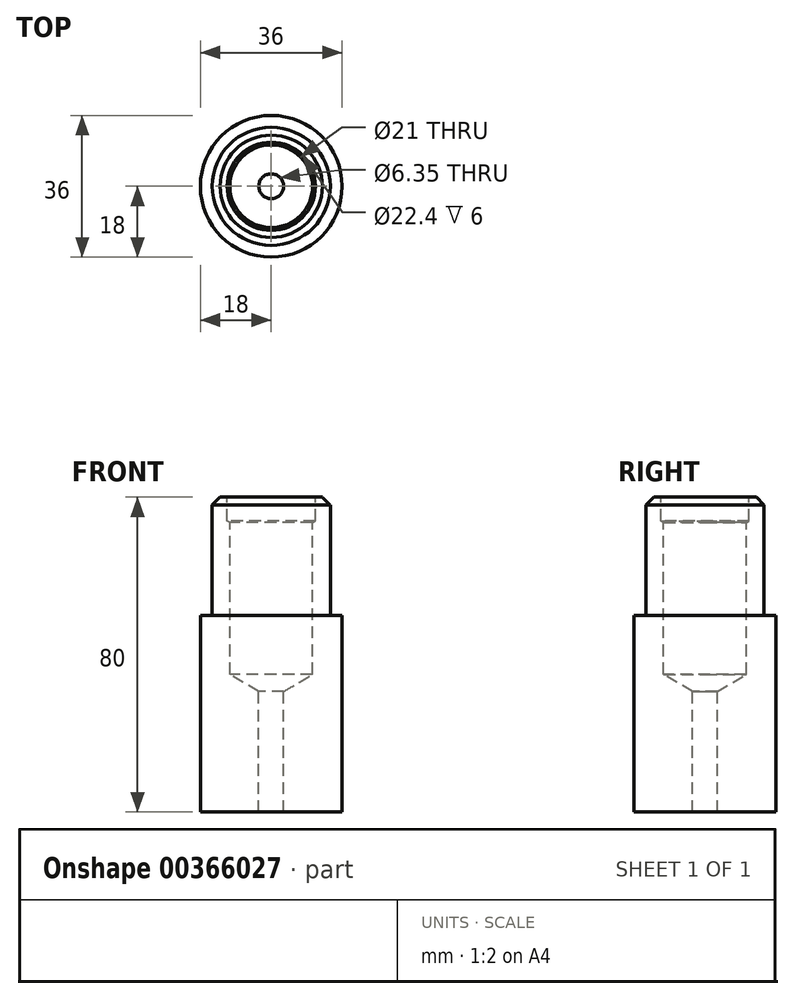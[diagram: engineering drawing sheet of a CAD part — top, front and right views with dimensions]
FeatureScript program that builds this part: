
annotation { "Feature Type Name" : "Feature", "Feature Type Description" : "" }
export const myFeature = defineFeature(function(context is Context, id is Id, definition is map)
    precondition{}
    {
        {
            var Q0;
            Q0=qCreatedBy(makeId("Top.planeOp"),FACE);
            var sketch = newSketch(context, id + "F0", { "sketchPlane" : qUnion([Q0])});
            skCircle(sketch, "E0", {"center": v(0, 0) * mm, "radius": 15 * mm});
            skSolve(sketch);
        }
        {
            var Q0;
            Q0=makeQuery(id+"F0.imprint","IMPRINT",FACE,{"disambiguationData":[TD([[makeQuery(id+"F0.imprint","IMPRINT",EDGE,{"derivedFrom":sQuery(id+"F0.wireOp",EDGE,"E0")}),1.0]])]});
            extrude(context, id + "F1", {"entities" : qUnion([Q0]), "depth" : 80 * mm});
        }
        {
            var Q0;
            Q0=qCreatedBy(makeId("Top.planeOp"),FACE);
            var sketch = newSketch(context, id + "F2", { "sketchPlane" : qUnion([Q0])});
            skCircle(sketch, "E1", {"center": v(0, 0) * mm, "radius": 18 * mm});
            skSolve(sketch);
        }
        {
            var Q0;
            Q0=makeQuery(id+"F2.imprint","IMPRINT",FACE,{"disambiguationData":[TD([[makeQuery(id+"F2.imprint","IMPRINT",EDGE,{"derivedFrom":sQuery(id+"F2.wireOp",EDGE,"E1")}),1.0]])]});
            extrude(context, id + "F3", {"entities" : qUnion([Q0]), "operationType" : NewBodyOperationType.ADD, "depth" : 50 * mm});
        }
        {
            var Q0;
            Q0=makeQuery(id+"F1.opExtrude","CAP_FACE",FACE,{"disambiguationData":[OSD([sQuery(id+"F0.wireOp",EDGE,"E0")])],"isStart":false});
            cPlane(context, id + "F4", {"entities" : qUnion([Q0]), "cplaneType" : CPlaneType.OFFSET, "offset" : 0 * mm, "width" : 150 * mm, "height" : 150 * mm});
        }
        {
            var Q0;
            Q0=qCreatedBy(id+"F4.planeOp",FACE);
            var sketch = newSketch(context, id + "F5", { "sketchPlane" : qUnion([Q0])});
            skPoint(sketch, "E2", {"position": v(0, 0) * mm});
            skSolve(sketch);
        }
        {
            var Q0;
            Q0=sQuery(id+"F5.wireOp",VERTEX,"E2");
            var Q1;
            Q1=makeQuery(id+"F1.opExtrude","SWEPT_BODY",BODY,{"disambiguationData":[OSD([sQuery(id+"F0.wireOp",EDGE,"E0")])]});
            hole(context, id + "F6", {"style" : HoleStyle.SIMPLE, "endStyle" : HoleEndStyle.THROUGH, "holeDiameter" : 6.35 * mm, "isTappedThrough" : true, "tappedDepth" : 12 * mm, "tapClearance" : 3, "startFromSketch" : true, "locations" : qUnion([Q0]), "scope" : qUnion([Q1])});
        }
        {
            var Q0;
            Q0=qCreatedBy(id+"F4.planeOp",FACE);
            var sketch = newSketch(context, id + "F7", { "sketchPlane" : qUnion([Q0])});
            skPoint(sketch, "E3", {"position": v(0, 0) * mm});
            skSolve(sketch);
        }
        {
            var Q0;
            Q0=sQuery(id+"F7.wireOp",VERTEX,"E3");
            var Q1;
            Q1=makeQuery(id+"F1.opExtrude","SWEPT_BODY",BODY,{"disambiguationData":[OSD([sQuery(id+"F0.wireOp",EDGE,"E0")])]});
            hole(context, id + "F8", {"style" : HoleStyle.SIMPLE, "endStyle" : HoleEndStyle.BLIND, "holeDiameter" : 21 * mm, "holeDepth" : 45 * mm, "isTappedThrough" : true, "tappedDepth" : 12 * mm, "tapClearance" : 3, "startFromSketch" : true, "locations" : qUnion([Q0]), "scope" : qUnion([Q1])});
        }
        {
            var Q0;
            Q0=qCreatedBy(id+"F4.planeOp",FACE);
            var sketch = newSketch(context, id + "F9", { "sketchPlane" : qUnion([Q0])});
            skPoint(sketch, "E4", {"position": v(0, 0) * mm});
            skSolve(sketch);
        }
        {
            var Q0;
            Q0=sQuery(id+"F9.wireOp",VERTEX,"E4");
            var Q1;
            Q1=makeQuery(id+"F1.opExtrude","SWEPT_BODY",BODY,{"disambiguationData":[OSD([sQuery(id+"F0.wireOp",EDGE,"E0")])]});
            hole(context, id + "F10", {"style" : HoleStyle.SIMPLE, "endStyle" : HoleEndStyle.BLIND, "holeDiameter" : 22.4 * mm, "holeDepth" : 6 * mm, "isTappedThrough" : true, "tappedDepth" : 12 * mm, "tapClearance" : 3, "startFromSketch" : true, "locations" : qUnion([Q0]), "scope" : qUnion([Q1])});
        }
        {
            var Q0;
            Q0=makeQuery(id+"F1.opExtrude","CAP_EDGE",EDGE,{"disambiguationData":[OSD([sQuery(id+"F0.wireOp",EDGE,"E0")])],"isStart":false});
            chamfer(context, id + "F11", {"entities" : qUnion([Q0]), "width" : 2 * mm, "tangentPropagation" : true});
        }
    });
